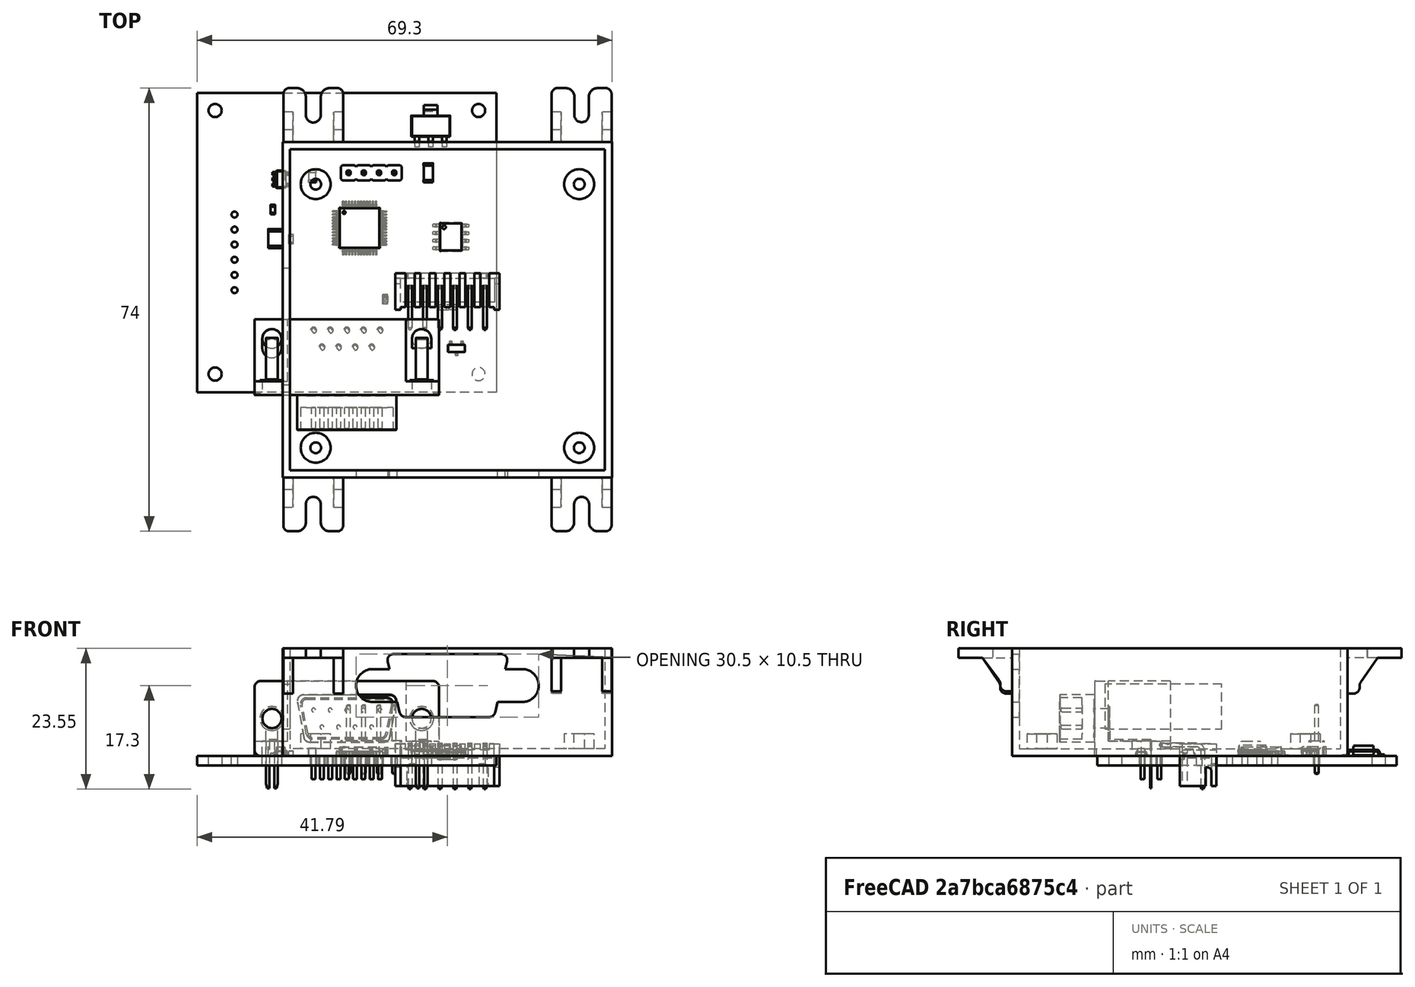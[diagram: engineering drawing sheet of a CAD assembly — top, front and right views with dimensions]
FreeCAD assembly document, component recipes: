
FREECAD ASSEMBLY — COMPONENT RECIPES ("CentralBox_Stuffed_JST")

This assembly document has 6 components, labeled P0..P5 below (a component is one placed body or linked part). 5 of them carry a construction recipe — the FreeCAD feature program that regenerates the part from scratch, quoted from this document or its linked companion documents; the rest are supplied as boundary geometry only. No exploded tour is included for this assembly.
COMPONENT P0 — geometry summary ("CTB-01.kicad_pro"; no construction recipe available for this part):
  bounding box: 56.3 x 51.1 x 17.9 mm
  tessellated surface: 81,650 triangles
  volume: 7482 mm^3 (15% of its bounding box)
COMPONENT P1 — recipe-attached ("Body", modeled in this document).
Construction recipe (the document's own serialized feature program — sketch geometry with constraints, then the solid features built on it; lengths are millimeters unless a unit is written):

FEATURE [Sketcher::SketchObject] Sketch
  FullyConstrained = true
  MapMode = 2
  Support = -> [XY_Plane]
  expr: Constraints[8] = <<Params>>.box_width_external
  expr: Constraints[9] = <<Params>>.box_length_external
  sketch-geometry (4):
    g0: LineSegment StartX=-27.5 StartY=28 StartZ=0 EndX=27.5 EndY=28 EndZ=0
    g1: LineSegment StartX=27.5 StartY=28 StartZ=0 EndX=27.5 EndY=-28 EndZ=0
    g2: LineSegment StartX=27.5 StartY=-28 StartZ=0 EndX=-27.5 EndY=-28 EndZ=0
    g3: LineSegment StartX=-27.5 StartY=-28 StartZ=0 EndX=-27.5 EndY=28 EndZ=0
  constraints (10):
    c: Coincident(g0,g1)
    c: Coincident(g1,g2)
    c: Coincident(g2,g3)
    c: Coincident(g3,g0)
    c: Horizontal(g2)
    c: Vertical(g3)
    c: Symmetric(g0,g1,g-1)
    c: Symmetric(g0,g0,g-2)
    c: DistanceY(g2,g0) = 56
    c: DistanceX(g0,g0) = 55
FEATURE [PartDesign::Pad] Pad
  Direction = (0,0,1)
  Length = 18
  Length2 = 10
  Profile = -> Sketch
  ReferenceAxis = -> Sketch [N_Axis]
  Type = 0
  expr: Length = <<Params>>.box_height
FEATURE [Sketcher::SketchObject] Sketch012
  FullyConstrained = true
  MapMode = 5
  Placement = pos=(0,0,18) rot=(0,0,1;0rad)
  Support = -> [Pad]
  expr: Constraints[8] = <<Params>>.box_length_internal
  expr: Constraints[9] = <<Params>>.box_width_internal
  sketch-geometry (4):
    g0: LineSegment StartX=-26.3 StartY=26.8 StartZ=0 EndX=26.3 EndY=26.8 EndZ=0
    g1: LineSegment StartX=26.3 StartY=26.8 StartZ=0 EndX=26.3 EndY=-26.8 EndZ=0
    g2: LineSegment StartX=26.3 StartY=-26.8 StartZ=0 EndX=-26.3 EndY=-26.8 EndZ=0
    g3: LineSegment StartX=-26.3 StartY=-26.8 StartZ=0 EndX=-26.3 EndY=26.8 EndZ=0
  constraints (10):
    c: Coincident(g0,g1)
    c: Coincident(g1,g2)
    c: Coincident(g2,g3)
    c: Coincident(g3,g0)
    c: Horizontal(g2)
    c: Vertical(g1)
    c: Symmetric(g0,g0,g-2)
    c: Symmetric(g0,g2,g-1)
    c: DistanceX(g0,g0) = 52.6
    c: DistanceY(g2,g0) = 53.6
FEATURE [PartDesign::Pocket] Pocket
  BaseFeature = -> Pad
  Direction = (0,0,-1)
  Length = 16.8
  Length2 = 5
  Profile = -> Sketch012
  ReferenceAxis = -> Sketch012 [N_Axis]
  Type = 0
  expr: Length = <<Params>>.box_depth
FEATURE [PartDesign::SubShapeBinder] Binder
  BindCopyOnChange = 0
  BindMode = 0
  ClaimChildren = false
  Context = -> Body [Binder.]
  Fuse = false
  MakeFace = true
  OffsetFill = false
  OffsetIntersection = false
  OffsetJoinType = 0
  OffsetOpenResult = false
  PartialLoad = false
  Relative = true
  _Version = 2
FEATURE [Sketcher::SketchObject] Sketch013
  ExternalGeometry = -> [Binder]
  FullyConstrained = true
  MapMode = 5
  Placement = pos=(0,-28,0) rot=(1,0,0;1.5708rad)
  Support = -> [Pocket]
  sketch-geometry (17):
    g0: ArcOfCircle CenterX=12.49 CenterY=11.75 CenterZ=0 NormalX=0 NormalY=0 NormalZ=1 AngleXU=0 Radius=2.75 StartAngle=4.70512 EndAngle=7.85398
    g1: ArcOfCircle CenterX=-12.51 CenterY=11.75 CenterZ=0 NormalX=0 NormalY=0 NormalZ=1 AngleXU=0 Radius=2.75 StartAngle=1.5708 EndAngle=4.71239
    g2: LineSegment StartX=-12.51 StartY=9 StartZ=0 EndX=-8.39 EndY=9 EndZ=0
    g3: LineSegment StartX=-12.51 StartY=14.5 StartZ=0 EndX=-9.68 EndY=14.5 EndZ=0
    g4: LineSegment StartX=-12.51 StartY=11.75 StartZ=0 EndX=12.49 EndY=11.75 EndZ=0
    g5: ArcOfCircle CenterX=-9.01 CenterY=16 CenterZ=0 NormalX=0 NormalY=0 NormalZ=1 AngleXU=0 Radius=1 StartAngle=1.5708 EndAngle=3.37594
    g6: ArcOfCircle CenterX=8.99 CenterY=16 CenterZ=0 NormalX=0 NormalY=0 NormalZ=1 AngleXU=0 Radius=1 StartAngle=6.04884 EndAngle=7.85398
    g7: ArcOfCircle CenterX=6.99 CenterY=7.5 CenterZ=0 NormalX=0 NormalY=0 NormalZ=1 AngleXU=0 Radius=1 StartAngle=4.71239 EndAngle=6.06326
    g8: ArcOfCircle CenterX=-7.01 CenterY=7.5 CenterZ=0 NormalX=0 NormalY=0 NormalZ=1 AngleXU=0 Radius=1 StartAngle=3.37255 EndAngle=4.71239
    g9: LineSegment StartX=-9.01 StartY=17 StartZ=0 EndX=8.99 EndY=17 EndZ=0
    g10: LineSegment StartX=6.99 StartY=6.5 StartZ=0 EndX=-7.01 EndY=6.5 EndZ=0
    g11: LineSegment StartX=-7.98345 StartY=7.27109 StartZ=0 EndX=-8.39 EndY=9 EndZ=0
    g12: LineSegment StartX=7.96591 StartY=7.28184 StartZ=0 EndX=8.35 EndY=9 EndZ=0
    g13: LineSegment StartX=9.66 StartY=14.5 StartZ=0 EndX=12.49 EndY=14.5 EndZ=0
    g14: LineSegment StartX=-9.68 StartY=14.5 StartZ=0 EndX=-9.98267 EndY=15.7678 EndZ=0
    g15: LineSegment StartX=8.35 StartY=9 StartZ=0 EndX=12.47 EndY=9.00007 EndZ=0
    g16: LineSegment StartX=9.66 StartY=14.5 StartZ=0 EndX=9.96267 EndY=15.7678 EndZ=0
  constraints (44):
    c: Coincident(g0,g-4)
    c: Coincident(g1,g-3)
    c: Diameter(g1) = 5.5
    c: Equal(g1,g0)
    c: Coincident(g4,g1)
    c: Coincident(g4,g0)
    c: Diameter(g6) = 2
    c: Equal(g6,g5)
    c: Equal(g5,g8)
    c: Equal(g8,g7)
    c: Horizontal(g9)
    c: Horizontal(g10)
    c: DistanceY(g10,g9) = 10.5
    c: DistanceX(g5,g6) = 18
    c: DistanceX(g8,g7) = 14
    c: DistanceX(g7,g0) = 5.5
    c: DistanceY(g7,g0) = 4.25
    c: DistanceX(g6,g0) = 3.5
    c: Tangent(g5,g9) = 1.5708
    c: Tangent(g6,g9) = 1.5708
    c: Tangent(g7,g12) = -1.5708
    c: Tangent(g7,g10) = 1.5708
    c: Tangent(g8,g10) = 1.5708
    c: Tangent(g8,g11) = 1.5708
    c: Tangent(g1,g3) = 1.5708
    c: Tangent(g1,g2) = -1.5708
    c: Coincident(g0,g15) = -1.5708
    c: Coincident(g0,g13) = 1.5708
    c: Coincident(g14,g3)
    c: Coincident(g2,g11)
    c: Coincident(g16,g13)
    c: Coincident(g12,g15)
    c: Horizontal(g2,g12)
    c: Horizontal(g3,g13)
    c: Equal(g13,g3)
    c: Equal(g2,g15)
    c: DistanceX(g2,g2) = 4.12
    c: DistanceX(g1,g3) = 2.83
    c: DistanceY(g1,g3) = 2.75
    c: DistanceY(g2,g1) = 2.75
    c: DistanceX(g13,g0) = 2.83
    c: DistanceX(g12,g0) = 4.14
    c: Tangent(g5,g14) = 1.5708
    c: Tangent(g6,g16) = -1.5708
FEATURE [PartDesign::Pocket] Pocket001
  BaseFeature = -> Pocket
  Direction = (0,1,-2e-16)
  Length = 5
  Length2 = 5
  Profile = -> Sketch013
  ReferenceAxis = -> Sketch013 [N_Axis]
  Type = 2
FEATURE [Sketcher::SketchObject] Sketch014
  FullyConstrained = true
  MapMode = 5
  Placement = pos=(-27.5,0,0) rot=(0.57735,-0.57735,-0.57735;2.0944rad)
  Support = -> [Pocket001]
  expr: Constraints[10] = <<Params>>.side_window_height
  expr: Constraints[11] = <<Params>>.side_window_y
  expr: Constraints[8] = <<Params>>.side_window_length
  expr: Constraints[9] = <<Params>>.side_window_z
  sketch-geometry (4):
    g0: LineSegment StartX=-7 StartY=12 StartZ=0 EndX=12.5 EndY=12 EndZ=0
    g1: LineSegment StartX=12.5 StartY=12 StartZ=0 EndX=12.5 EndY=4.5 EndZ=0
    g2: LineSegment StartX=12.5 StartY=4.5 StartZ=0 EndX=-7 EndY=4.5 EndZ=0
    g3: LineSegment StartX=-7 StartY=4.5 StartZ=0 EndX=-7 EndY=12 EndZ=0
  constraints (12):
    c: Coincident(g0,g1)
    c: Coincident(g1,g2)
    c: Coincident(g2,g3)
    c: Coincident(g3,g0)
    c: Horizontal(g0)
    c: Horizontal(g2)
    c: Vertical(g1)
    c: Vertical(g3)
    c: DistanceX(g2,g1) = 19.5
    c: DistanceY(g-1,g2) = 4.5
    c: DistanceY(g2,g0) = 7.5
    c: DistanceX(g-1,g1) = 12.5
FEATURE [PartDesign::Pocket] Pocket002
  BaseFeature = -> Pocket001
  Direction = (1,0,0)
  Length = 5
  Length2 = 5
  Profile = -> Sketch014
  ReferenceAxis = -> Sketch014 [N_Axis]
  Type = 2
FEATURE [PartDesign::SubShapeBinder] Binder001
  BindCopyOnChange = 0
  BindMode = 0
  ClaimChildren = false
  Context = -> Body [Binder001.]
  Fuse = false
  MakeFace = true
  OffsetFill = false
  OffsetIntersection = false
  OffsetJoinType = 0
  OffsetOpenResult = false
  PartialLoad = false
  Relative = true
  _Version = 2
FEATURE [Sketcher::SketchObject] Sketch015
  ExternalGeometry = -> [Binder001]
  FullyConstrained = true
  MapMode = 5
  Placement = pos=(0,0,1.2) rot=(0,0,1;0rad)
  Support = -> [Pocket002]
  expr: Constraints[8] = <<Params>>.monting_boss_hole
  expr: Constraints[9] = <<Params>>.mounting_boss_pad
  sketch-geometry (8):
    g0: Circle CenterX=22 CenterY=-23.05 CenterZ=0 NormalX=0 NormalY=0 NormalZ=1 AngleXU=0 Radius=0.9
    g1: Circle CenterX=22 CenterY=-23.05 CenterZ=0 NormalX=0 NormalY=0 NormalZ=1 AngleXU=0 Radius=2.5
    g2: Circle CenterX=-22 CenterY=-23.05 CenterZ=0 NormalX=0 NormalY=0 NormalZ=1 AngleXU=0 Radius=0.9
    g3: Circle CenterX=-22 CenterY=-23.05 CenterZ=0 NormalX=0 NormalY=0 NormalZ=1 AngleXU=0 Radius=2.5
    g4: Circle CenterX=22 CenterY=20.95 CenterZ=0 NormalX=0 NormalY=0 NormalZ=1 AngleXU=0 Radius=0.9
    g5: Circle CenterX=22 CenterY=20.95 CenterZ=0 NormalX=0 NormalY=0 NormalZ=1 AngleXU=0 Radius=2.5
    g6: Circle CenterX=-22 CenterY=20.95 CenterZ=0 NormalX=0 NormalY=0 NormalZ=1 AngleXU=0 Radius=0.9
    g7: Circle CenterX=-22 CenterY=20.95 CenterZ=0 NormalX=0 NormalY=0 NormalZ=1 AngleXU=0 Radius=2.5
  constraints (16):
    c: Coincident(g0,g-5)
    c: Coincident(g1,g0)
    c: Coincident(g2,g-6)
    c: Coincident(g3,g2)
    c: Coincident(g4,g-4)
    c: Coincident(g5,g4)
    c: Coincident(g6,g-3)
    c: Coincident(g7,g6)
    c: Diameter(g4) = 1.8
    c: Diameter(g5) = 5
    c: Equal(g4,g2)
    c: Equal(g2,g0)
    c: Equal(g4,g6)
    c: Equal(g5,g7)
    c: Equal(g7,g1)
    c: Equal(g1,g3)
FEATURE [PartDesign::Pad] Pad010
  BaseFeature = -> Pocket002
  Direction = (0,0,1)
  Length = 2.5
  Length2 = 10
  Profile = -> Sketch015
  ReferenceAxis = -> Sketch015 [N_Axis]
  Type = 0
  expr: Length = <<Params>>.mounting_boss_height
FEATURE [PartDesign::Body] Body
  Group = -> [Sketch,Pad,Sketch012,Pocket,Binder,Sketch013,Pocket001,Sketch014,Pocket002,Binder001,Sketch015,Pad010]
  Origin = -> Origin
  Tip = -> Pad010
COMPONENT P2 — recipe-attached ("Tab1", modeled in this document).
Construction recipe (the document's own serialized feature program — sketch geometry with constraints, then the solid features built on it; lengths are millimeters unless a unit is written):

FEATURE [Sketcher::SketchObject] Sketch004
  FullyConstrained = true
  MapMode = 5
  Support = -> [XY_Plane009]
  expr: Constraints[13] = <<Params001>>.tab_length
  expr: Constraints[14] = <<Params001>>.tab_width
  expr: Constraints[19] = <<Params001>>.tab_hole_diameter
  expr: Constraints[20] = <<Params001>>.tab_hole_x
  sketch-geometry (8):
    g0: LineSegment StartX=-4.5 StartY=5 StartZ=0 EndX=4.5 EndY=5 EndZ=0
    g1: LineSegment StartX=4.5 StartY=5 StartZ=0 EndX=4.5 EndY=1.25 EndZ=0
    g2: LineSegment StartX=4.5 StartY=-5 StartZ=0 EndX=-4.5 EndY=-5 EndZ=0
    g3: LineSegment StartX=-4.5 StartY=-5 StartZ=0 EndX=-4.5 EndY=5 EndZ=0
    g4: ArcOfCircle CenterX=-1e-16 CenterY=0 CenterZ=0 NormalX=0 NormalY=0 NormalZ=1 AngleXU=0 Radius=1.25 StartAngle=1.5708 EndAngle=4.71239
    g5: LineSegment StartX=-3e-16 StartY=1.25 StartZ=0 EndX=4.5 EndY=1.25 EndZ=0
    g6: LineSegment StartX=4.5 StartY=-1.25 StartZ=0 EndX=0 EndY=-1.25 EndZ=0
    g7: LineSegment StartX=4.5 StartY=-1.25 StartZ=0 EndX=4.5 EndY=-5 EndZ=0
  constraints (21):
    c: Coincident(g0,g1)
    c: Coincident(g7,g2)
    c: Coincident(g2,g3)
    c: Coincident(g3,g0)
    c: Horizontal(g2)
    c: Vertical(g1)
    c: Symmetric(g0,g0,g-2)
    c: Symmetric(g0,g2,g-1)
    c: PointOnObject(g4,g-1)
    c: Horizontal(g5)
    c: Horizontal(g6)
    c: Coincident(g1,g5)
    c: Coincident(g7,g6)
    c: DistanceX(g0,g0) = 9
    c: DistanceY(g2,g0) = 10
    c: Tangent(g4,g5) = 1.5708
    c: Tangent(g6,g4) = 1.5708
    c: Vertical(g7)
    c: Vertical(g6,g1)
    c: Diameter(g4) = 2.5
    c: DistanceX(g0,g4) = 4.5
FEATURE [PartDesign::Pad] Pad002
  Direction = (0,0,1)
  Length = 1.6
  Length2 = 10
  Profile = -> Sketch004
  ReferenceAxis = -> Sketch004 [N_Axis]
  Type = 0
  expr: Length = <<Params001>>.tab_thickness
FEATURE [PartDesign::Plane] DatumPlane002  label="PlaneRib"
  Length = 60
  MapMode = 5
  Placement = pos=(0,-5,0) rot=(1,0,0;1.5708rad)
  ResizeMode = 0
  Support = -> [Pad002]
  Width = 60
FEATURE [Sketcher::SketchObject] Sketch005
  ExternalGeometry = -> [Pad002]
  FullyConstrained = true
  MapMode = 5
  Placement = pos=(0,-5,0) rot=(1,0,0;1.5708rad)
  Support = -> [DatumPlane002]
  expr: Constraints[11] = <<Params001>>.tab_rib_height
  expr: Constraints[12] = <<Params001>>.tab_rib_length
  expr: Constraints[13] = <<Params001>>.tab_rib_insert
  expr: Constraints[6] = <<Params001>>.tab_height
  sketch-geometry (5):
    g0: LineSegment StartX=-4.5 StartY=0 StartZ=0 EndX=-4.5 EndY=-5.6 EndZ=0
    g1: LineSegment StartX=-4.5 StartY=-5.6 StartZ=0 EndX=-2.5 EndY=-5.6 EndZ=0
    g2: LineSegment StartX=0.5 StartY=0 StartZ=0 EndX=-4.5 EndY=0 EndZ=0
    g3: LineSegment StartX=-2.5 StartY=-5.6 StartZ=0 EndX=-2.5 EndY=-4 EndZ=0
    g4: LineSegment StartX=-2.5 StartY=-4 StartZ=0 EndX=0.5 EndY=0 EndZ=0
  constraints (14):
    c: Coincident(g0,g-3)
    c: Vertical(g0)
    c: Coincident(g1,g0)
    c: PointOnObject(g2,g-1)
    c: Coincident(g2,g0)
    c: Horizontal(g1)
    c: DistanceY(g0,g0) = 5.6
    c: Coincident(g3,g1)
    c: Vertical(g3)
    c: Coincident(g4,g3)
    c: Coincident(g4,g2)
    c: DistanceY(g3,g-1) = 4
    c: DistanceX(g0,g2) = 5
    c: DistanceX(g0,g1) = 2
FEATURE [PartDesign::Pad] Pad003  label="TabRib1"
  BaseFeature = -> Pad002
  Direction = (0,-1,2e-16)
  Length = 1.6
  Length2 = 10
  Profile = -> Sketch005
  ReferenceAxis = -> Sketch005 [N_Axis]
  Reversed = true
  Type = 0
  expr: Length = <<Params001>>.tab_rib_thickness
FEATURE [PartDesign::LinearPattern] LinearPattern  label="TabRib2"
  BaseFeature = -> Pad003
  Direction = -> Y_Axis009
  Length = 8.4
  Occurrences = 2
  Originals = -> [Pad003]
  expr: Length = <<Params001>>.tab_ribs_gap
FEATURE [PartDesign::Fillet] Fillet
  Base = -> LinearPattern [Edge51,Edge52]
  BaseFeature = -> LinearPattern
  Radius = 1
  SupportTransform = false
  UseAllEdges = false
FEATURE [PartDesign::Fillet] Fillet001
  Base = -> Fillet [Edge14,Edge52]
  BaseFeature = -> Fillet
  Radius = 1
  SupportTransform = false
  UseAllEdges = false
FEATURE [PartDesign::Fillet] Fillet002
  Base = -> Fillet001 [Edge19,Edge53]
  BaseFeature = -> Fillet001
  Radius = 1
  SupportTransform = false
  UseAllEdges = false
FEATURE [PartDesign::Fillet] Fillet003
  Base = -> Fillet002 [Edge38,Edge43]
  BaseFeature = -> Fillet002
  Radius = 1.5
  SupportTransform = false
  UseAllEdges = false
FEATURE [PartDesign::Body] Body001  label="Tab1"
  Group = -> [Sketch004,Pad002,DatumPlane002,Sketch005,Pad003,LinearPattern,Fillet,Fillet001,Fillet002,Fillet003]
  Origin = -> Origin009
  Placement = pos=(22.4,-32.5,16.4) rot=(0,0,-1;1.5708rad)
  Tip = -> Fillet003
COMPONENT P3 — recipe-attached ("Tab2", modeled in this document).
Construction recipe (the document's own serialized feature program — sketch geometry with constraints, then the solid features built on it; lengths are millimeters unless a unit is written):

FEATURE [Sketcher::SketchObject] Sketch006
  FullyConstrained = true
  MapMode = 5
  Support = -> [XY_Plane010]
  expr: Constraints[13] = <<Params002>>.tab_length
  expr: Constraints[14] = <<Params002>>.tab_width
  expr: Constraints[19] = <<Params002>>.tab_hole_diameter
  expr: Constraints[20] = <<Params002>>.tab_hole_x
  sketch-geometry (8):
    g0: LineSegment StartX=-4.5 StartY=5 StartZ=0 EndX=4.5 EndY=5 EndZ=0
    g1: LineSegment StartX=4.5 StartY=5 StartZ=0 EndX=4.5 EndY=1.2 EndZ=0
    g2: LineSegment StartX=4.5 StartY=-5 StartZ=0 EndX=-4.5 EndY=-5 EndZ=0
    g3: LineSegment StartX=-4.5 StartY=-5 StartZ=0 EndX=-4.5 EndY=5 EndZ=0
    g4: ArcOfCircle CenterX=-3e-16 CenterY=0 CenterZ=0 NormalX=0 NormalY=0 NormalZ=1 AngleXU=0 Radius=1.2 StartAngle=1.5708 EndAngle=4.71239
    g5: LineSegment StartX=-5e-16 StartY=1.2 StartZ=0 EndX=4.5 EndY=1.2 EndZ=0
    g6: LineSegment StartX=4.5 StartY=-1.2 StartZ=0 EndX=-9e-16 EndY=-1.2 EndZ=0
    g7: LineSegment StartX=4.5 StartY=-1.2 StartZ=0 EndX=4.5 EndY=-5 EndZ=0
  constraints (21):
    c: Coincident(g0,g1)
    c: Coincident(g7,g2)
    c: Coincident(g2,g3)
    c: Coincident(g3,g0)
    c: Horizontal(g2)
    c: Vertical(g1)
    c: Symmetric(g0,g0,g-2)
    c: Symmetric(g0,g2,g-1)
    c: PointOnObject(g4,g-1)
    c: Horizontal(g5)
    c: Horizontal(g6)
    c: Coincident(g1,g5)
    c: Coincident(g7,g6)
    c: DistanceX(g0,g0) = 9
    c: DistanceY(g2,g0) = 10
    c: Tangent(g4,g5) = 1.5708
    c: Tangent(g6,g4) = 1.5708
    c: Vertical(g7)
    c: Vertical(g6,g1)
    c: Diameter(g4) = 2.4
    c: DistanceX(g0,g4) = 4.5
FEATURE [PartDesign::Pad] Pad004
  Direction = (0,0,1)
  Length = 1.6
  Length2 = 10
  Profile = -> Sketch006
  ReferenceAxis = -> Sketch006 [N_Axis]
  Type = 0
  expr: Length = <<Params002>>.tab_thickness
FEATURE [PartDesign::Plane] DatumPlane003  label="PlaneRib001"
  Length = 60
  MapMode = 5
  Placement = pos=(0,-5,0) rot=(1,0,0;1.5708rad)
  ResizeMode = 0
  Support = -> [Pad004]
  Width = 60
FEATURE [Sketcher::SketchObject] Sketch007
  ExternalGeometry = -> [Pad004]
  FullyConstrained = true
  MapMode = 5
  Placement = pos=(0,-5,0) rot=(1,0,0;1.5708rad)
  Support = -> [DatumPlane003]
  expr: Constraints[11] = <<Params002>>.tab_rib_height
  expr: Constraints[12] = <<Params002>>.tab_rib_length
  expr: Constraints[13] = <<Params002>>.tab_rib_insert
  expr: Constraints[6] = <<Params002>>.tab_height
  sketch-geometry (5):
    g0: LineSegment StartX=-4.5 StartY=0 StartZ=0 EndX=-4.5 EndY=-6 EndZ=0
    g1: LineSegment StartX=-4.5 StartY=-6 StartZ=0 EndX=-2.5 EndY=-6 EndZ=0
    g2: LineSegment StartX=0.5 StartY=0 StartZ=0 EndX=-4.5 EndY=0 EndZ=0
    g3: LineSegment StartX=-2.5 StartY=-6 StartZ=0 EndX=-2.5 EndY=-4.4 EndZ=0
    g4: LineSegment StartX=-2.5 StartY=-4.4 StartZ=0 EndX=0.5 EndY=0 EndZ=0
  constraints (14):
    c: Coincident(g0,g-3)
    c: Vertical(g0)
    c: Coincident(g1,g0)
    c: PointOnObject(g2,g-1)
    c: Coincident(g2,g0)
    c: Horizontal(g1)
    c: DistanceY(g0,g0) = 6
    c: Coincident(g3,g1)
    c: Vertical(g3)
    c: Coincident(g4,g3)
    c: Coincident(g4,g2)
    c: DistanceY(g3,g-1) = 4.4
    c: DistanceX(g0,g2) = 5
    c: DistanceX(g0,g1) = 2
FEATURE [PartDesign::Pad] Pad005  label="TabRib004"
  BaseFeature = -> Pad004
  Direction = (0,-1,2e-16)
  Length = 1.6
  Length2 = 10
  Profile = -> Sketch007
  ReferenceAxis = -> Sketch007 [N_Axis]
  Reversed = true
  Type = 0
  expr: Length = <<Params002>>.tab_rib_thickness
FEATURE [PartDesign::LinearPattern] LinearPattern001  label="TabRib003"
  BaseFeature = -> Pad005
  Direction = -> Y_Axis010
  Length = 8.4
  Occurrences = 2
  Originals = -> [Pad005]
  expr: Length = <<Params002>>.tab_ribs_gap
FEATURE [PartDesign::Fillet] Fillet004
  Base = -> LinearPattern001 [Edge51,Edge52]
  BaseFeature = -> LinearPattern001
  Radius = 1
  SupportTransform = false
  UseAllEdges = false
FEATURE [PartDesign::Fillet] Fillet005
  Base = -> Fillet004 [Edge14,Edge52]
  BaseFeature = -> Fillet004
  Radius = 1
  SupportTransform = false
  UseAllEdges = false
FEATURE [PartDesign::Fillet] Fillet006
  Base = -> Fillet005 [Edge19,Edge53]
  BaseFeature = -> Fillet005
  Radius = 1
  SupportTransform = false
  UseAllEdges = false
FEATURE [PartDesign::Fillet] Fillet007
  Base = -> Fillet006 [Edge38,Edge43]
  BaseFeature = -> Fillet006
  Radius = 1.5
  SupportTransform = false
  UseAllEdges = false
FEATURE [PartDesign::Body] Body002  label="Tab2"
  Group = -> [Sketch006,Pad004,DatumPlane003,Sketch007,Pad005,LinearPattern001,Fillet004,Fillet005,Fillet006,Fillet007]
  Origin = -> Origin010
  Placement = pos=(22.4,32.5,16.4) rot=(0,0,1;1.5708rad)
  Tip = -> Fillet007
COMPONENT P4 — recipe-attached ("Tab3", modeled in this document).
Construction recipe (the document's own serialized feature program — sketch geometry with constraints, then the solid features built on it; lengths are millimeters unless a unit is written):

FEATURE [Sketcher::SketchObject] Sketch008
  FullyConstrained = true
  MapMode = 5
  Support = -> [XY_Plane011]
  expr: Constraints[13] = <<Params003>>.tab_length
  expr: Constraints[14] = <<Params003>>.tab_width
  expr: Constraints[19] = <<Params003>>.tab_hole_diameter
  expr: Constraints[20] = <<Params003>>.tab_hole_x
  sketch-geometry (8):
    g0: LineSegment StartX=-4.5 StartY=5 StartZ=0 EndX=4.5 EndY=5 EndZ=0
    g1: LineSegment StartX=4.5 StartY=5 StartZ=0 EndX=4.5 EndY=1.25 EndZ=0
    g2: LineSegment StartX=4.5 StartY=-5 StartZ=0 EndX=-4.5 EndY=-5 EndZ=0
    g3: LineSegment StartX=-4.5 StartY=-5 StartZ=0 EndX=-4.5 EndY=5 EndZ=0
    g4: ArcOfCircle CenterX=-1e-16 CenterY=0 CenterZ=0 NormalX=0 NormalY=0 NormalZ=1 AngleXU=0 Radius=1.25 StartAngle=1.5708 EndAngle=4.71239
    g5: LineSegment StartX=-3e-16 StartY=1.25 StartZ=0 EndX=4.5 EndY=1.25 EndZ=0
    g6: LineSegment StartX=4.5 StartY=-1.25 StartZ=0 EndX=0 EndY=-1.25 EndZ=0
    g7: LineSegment StartX=4.5 StartY=-1.25 StartZ=0 EndX=4.5 EndY=-5 EndZ=0
  constraints (21):
    c: Coincident(g0,g1)
    c: Coincident(g7,g2)
    c: Coincident(g2,g3)
    c: Coincident(g3,g0)
    c: Horizontal(g2)
    c: Vertical(g1)
    c: Symmetric(g0,g0,g-2)
    c: Symmetric(g0,g2,g-1)
    c: PointOnObject(g4,g-1)
    c: Horizontal(g5)
    c: Horizontal(g6)
    c: Coincident(g1,g5)
    c: Coincident(g7,g6)
    c: DistanceX(g0,g0) = 9
    c: DistanceY(g2,g0) = 10
    c: Tangent(g4,g5) = 1.5708
    c: Tangent(g6,g4) = 1.5708
    c: Vertical(g7)
    c: Vertical(g6,g1)
    c: Diameter(g4) = 2.5
    c: DistanceX(g0,g4) = 4.5
FEATURE [PartDesign::Pad] Pad006
  Direction = (0,0,1)
  Length = 1.6
  Length2 = 10
  Profile = -> Sketch008
  ReferenceAxis = -> Sketch008 [N_Axis]
  Type = 0
  expr: Length = <<Params003>>.tab_thickness
FEATURE [PartDesign::Plane] DatumPlane004  label="PlaneRib002"
  Length = 60
  MapMode = 5
  Placement = pos=(0,-5,0) rot=(1,0,0;1.5708rad)
  ResizeMode = 0
  Support = -> [Pad006]
  Width = 60
FEATURE [Sketcher::SketchObject] Sketch009
  ExternalGeometry = -> [Pad006]
  FullyConstrained = true
  MapMode = 5
  Placement = pos=(0,-5,0) rot=(1,0,0;1.5708rad)
  Support = -> [DatumPlane004]
  expr: Constraints[11] = <<Params003>>.tab_rib_height
  expr: Constraints[12] = <<Params003>>.tab_rib_length
  expr: Constraints[13] = <<Params003>>.tab_rib_insert
  expr: Constraints[6] = <<Params003>>.tab_height
  sketch-geometry (5):
    g0: LineSegment StartX=-4.5 StartY=0 StartZ=0 EndX=-4.5 EndY=-6 EndZ=0
    g1: LineSegment StartX=-4.5 StartY=-6 StartZ=0 EndX=-2.5 EndY=-6 EndZ=0
    g2: LineSegment StartX=0.5 StartY=0 StartZ=0 EndX=-4.5 EndY=0 EndZ=0
    g3: LineSegment StartX=-2.5 StartY=-6 StartZ=0 EndX=-2.5 EndY=-4.4 EndZ=0
    g4: LineSegment StartX=-2.5 StartY=-4.4 StartZ=0 EndX=0.5 EndY=0 EndZ=0
  constraints (14):
    c: Coincident(g0,g-3)
    c: Vertical(g0)
    c: Coincident(g1,g0)
    c: PointOnObject(g2,g-1)
    c: Coincident(g2,g0)
    c: Horizontal(g1)
    c: DistanceY(g0,g0) = 6
    c: Coincident(g3,g1)
    c: Vertical(g3)
    c: Coincident(g4,g3)
    c: Coincident(g4,g2)
    c: DistanceY(g3,g-1) = 4.4
    c: DistanceX(g0,g2) = 5
    c: DistanceX(g0,g1) = 2
FEATURE [PartDesign::Pad] Pad007  label="TabRib006"
  BaseFeature = -> Pad006
  Direction = (0,-1,2e-16)
  Length = 1.6
  Length2 = 10
  Profile = -> Sketch009
  ReferenceAxis = -> Sketch009 [N_Axis]
  Reversed = true
  Type = 0
  expr: Length = <<Params003>>.tab_rib_thickness
FEATURE [PartDesign::LinearPattern] LinearPattern002  label="TabRib005"
  BaseFeature = -> Pad007
  Direction = -> Y_Axis011
  Length = 8.4
  Occurrences = 2
  Originals = -> [Pad007]
  expr: Length = <<Params003>>.tab_ribs_gap
FEATURE [PartDesign::Fillet] Fillet008
  Base = -> LinearPattern002 [Edge51,Edge52]
  BaseFeature = -> LinearPattern002
  Radius = 1
  SupportTransform = false
  UseAllEdges = false
FEATURE [PartDesign::Fillet] Fillet009
  Base = -> Fillet008 [Edge14,Edge52]
  BaseFeature = -> Fillet008
  Radius = 1
  SupportTransform = false
  UseAllEdges = false
FEATURE [PartDesign::Fillet] Fillet010
  Base = -> Fillet009 [Edge19,Edge53]
  BaseFeature = -> Fillet009
  Radius = 1
  SupportTransform = false
  UseAllEdges = false
FEATURE [PartDesign::Fillet] Fillet011
  Base = -> Fillet010 [Edge38,Edge43]
  BaseFeature = -> Fillet010
  Radius = 1.5
  SupportTransform = false
  UseAllEdges = false
FEATURE [PartDesign::Body] Body003  label="Tab3"
  Group = -> [Sketch008,Pad006,DatumPlane004,Sketch009,Pad007,LinearPattern002,Fillet008,Fillet009,Fillet010,Fillet011]
  Origin = -> Origin011
  Placement = pos=(-22.4,32.5,16.4) rot=(0,0,1;1.5708rad)
  Tip = -> Fillet011
COMPONENT P5 — recipe-attached ("Tab4", modeled in this document).
Construction recipe (the document's own serialized feature program — sketch geometry with constraints, then the solid features built on it; lengths are millimeters unless a unit is written):

FEATURE [Sketcher::SketchObject] Sketch010
  FullyConstrained = true
  MapMode = 5
  Support = -> [XY_Plane012]
  expr: Constraints[13] = <<Params004>>.tab_length
  expr: Constraints[14] = <<Params004>>.tab_width
  expr: Constraints[19] = <<Params004>>.tab_hole_diameter
  expr: Constraints[20] = <<Params004>>.tab_hole_x
  sketch-geometry (8):
    g0: LineSegment StartX=-4.5 StartY=5 StartZ=0 EndX=4.5 EndY=5 EndZ=0
    g1: LineSegment StartX=4.5 StartY=5 StartZ=0 EndX=4.5 EndY=1.25 EndZ=0
    g2: LineSegment StartX=4.5 StartY=-5 StartZ=0 EndX=-4.5 EndY=-5 EndZ=0
    g3: LineSegment StartX=-4.5 StartY=-5 StartZ=0 EndX=-4.5 EndY=5 EndZ=0
    g4: ArcOfCircle CenterX=-3e-16 CenterY=0 CenterZ=0 NormalX=0 NormalY=0 NormalZ=1 AngleXU=0 Radius=1.25 StartAngle=1.5708 EndAngle=4.71239
    g5: LineSegment StartX=-5e-16 StartY=1.25 StartZ=0 EndX=4.5 EndY=1.25 EndZ=0
    g6: LineSegment StartX=4.5 StartY=-1.25 StartZ=0 EndX=-9e-16 EndY=-1.25 EndZ=0
    g7: LineSegment StartX=4.5 StartY=-1.25 StartZ=0 EndX=4.5 EndY=-5 EndZ=0
  constraints (21):
    c: Coincident(g0,g1)
    c: Coincident(g7,g2)
    c: Coincident(g2,g3)
    c: Coincident(g3,g0)
    c: Horizontal(g2)
    c: Vertical(g1)
    c: Symmetric(g0,g0,g-2)
    c: Symmetric(g0,g2,g-1)
    c: PointOnObject(g4,g-1)
    c: Horizontal(g5)
    c: Horizontal(g6)
    c: Coincident(g1,g5)
    c: Coincident(g7,g6)
    c: DistanceX(g0,g0) = 9
    c: DistanceY(g2,g0) = 10
    c: Tangent(g4,g5) = 1.5708
    c: Tangent(g6,g4) = 1.5708
    c: Vertical(g7)
    c: Vertical(g6,g1)
    c: Diameter(g4) = 2.5
    c: DistanceX(g0,g4) = 4.5
FEATURE [PartDesign::Pad] Pad008
  Direction = (0,0,1)
  Length = 1.6
  Length2 = 10
  Profile = -> Sketch010
  ReferenceAxis = -> Sketch010 [N_Axis]
  Type = 0
  expr: Length = <<Params004>>.tab_thickness
FEATURE [PartDesign::Plane] DatumPlane005  label="PlaneRib003"
  Length = 60
  MapMode = 5
  Placement = pos=(0,-5,0) rot=(1,0,0;1.5708rad)
  ResizeMode = 0
  Support = -> [Pad008]
  Width = 60
FEATURE [Sketcher::SketchObject] Sketch011
  ExternalGeometry = -> [Pad008]
  FullyConstrained = true
  MapMode = 5
  Placement = pos=(0,-5,0) rot=(1,0,0;1.5708rad)
  Support = -> [DatumPlane005]
  expr: Constraints[11] = <<Params004>>.tab_rib_height
  expr: Constraints[12] = <<Params004>>.tab_rib_length
  expr: Constraints[13] = <<Params004>>.tab_rib_insert
  expr: Constraints[6] = <<Params004>>.tab_height
  sketch-geometry (5):
    g0: LineSegment StartX=-4.5 StartY=0 StartZ=0 EndX=-4.5 EndY=-6 EndZ=0
    g1: LineSegment StartX=-4.5 StartY=-6 StartZ=0 EndX=-2.5 EndY=-6 EndZ=0
    g2: LineSegment StartX=0.5 StartY=0 StartZ=0 EndX=-4.5 EndY=0 EndZ=0
    g3: LineSegment StartX=-2.5 StartY=-6 StartZ=0 EndX=-2.5 EndY=-4.4 EndZ=0
    g4: LineSegment StartX=-2.5 StartY=-4.4 StartZ=0 EndX=0.5 EndY=0 EndZ=0
  constraints (14):
    c: Coincident(g0,g-3)
    c: Vertical(g0)
    c: Coincident(g1,g0)
    c: PointOnObject(g2,g-1)
    c: Coincident(g2,g0)
    c: Horizontal(g1)
    c: DistanceY(g0,g0) = 6
    c: Coincident(g3,g1)
    c: Vertical(g3)
    c: Coincident(g4,g3)
    c: Coincident(g4,g2)
    c: DistanceY(g3,g-1) = 4.4
    c: DistanceX(g0,g2) = 5
    c: DistanceX(g0,g1) = 2
FEATURE [PartDesign::Pad] Pad009  label="TabRib008"
  BaseFeature = -> Pad008
  Direction = (0,-1,2e-16)
  Length = 1.6
  Length2 = 10
  Profile = -> Sketch011
  ReferenceAxis = -> Sketch011 [N_Axis]
  Reversed = true
  Type = 0
  expr: Length = <<Params004>>.tab_rib_thickness
FEATURE [PartDesign::LinearPattern] LinearPattern003  label="TabRib007"
  BaseFeature = -> Pad009
  Direction = -> Y_Axis012
  Length = 8.4
  Occurrences = 2
  Originals = -> [Pad009]
  expr: Length = <<Params004>>.tab_ribs_gap
FEATURE [PartDesign::Fillet] Fillet012
  Base = -> LinearPattern003 [Edge51,Edge52]
  BaseFeature = -> LinearPattern003
  Radius = 1
  SupportTransform = false
  UseAllEdges = false
FEATURE [PartDesign::Fillet] Fillet013
  Base = -> Fillet012 [Edge14,Edge52]
  BaseFeature = -> Fillet012
  Radius = 1
  SupportTransform = false
  UseAllEdges = false
FEATURE [PartDesign::Fillet] Fillet014
  Base = -> Fillet013 [Edge19,Edge53]
  BaseFeature = -> Fillet013
  Radius = 1
  SupportTransform = false
  UseAllEdges = false
FEATURE [PartDesign::Fillet] Fillet015
  Base = -> Fillet014 [Edge38,Edge43]
  BaseFeature = -> Fillet014
  Radius = 1.5
  SupportTransform = false
  UseAllEdges = false
FEATURE [PartDesign::Body] Body004  label="Tab4"
  Group = -> [Sketch010,Pad008,DatumPlane005,Sketch011,Pad009,LinearPattern003,Fillet012,Fillet013,Fillet014,Fillet015]
  Origin = -> Origin012
  Placement = pos=(-22.4,-32.5,16.4) rot=(0,0,-1;1.5708rad)
  Tip = -> Fillet015
PROVENANCE & LICENSES
A FreeCAD (.FCStd) document from a public repository crawl; recipes are the document's own serialized feature recipes (and, for linked parts, companion documents' recipes).
License: as declared in the source repository (recorded in the dataset sidecar).
